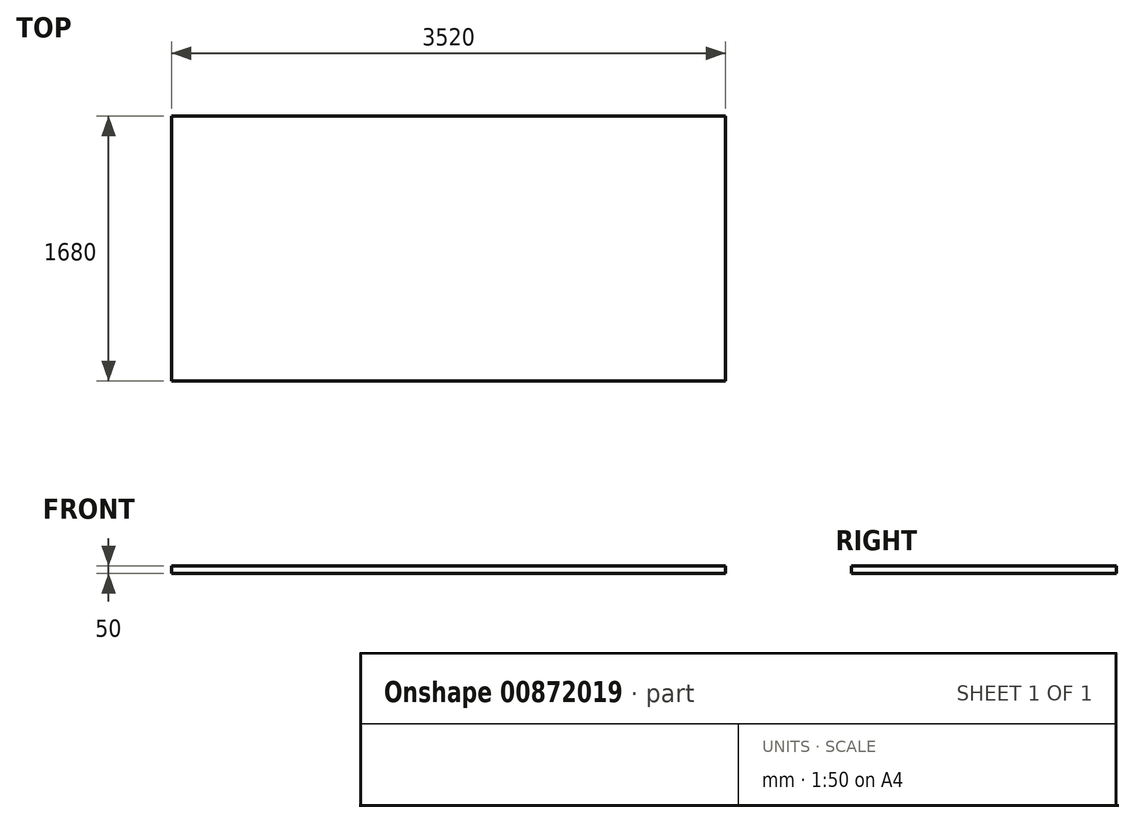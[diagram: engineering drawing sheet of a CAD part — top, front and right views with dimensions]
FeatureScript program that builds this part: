
annotation { "Feature Type Name" : "Feature", "Feature Type Description" : "" }
export const myFeature = defineFeature(function(context is Context, id is Id, definition is map)
    precondition{}
    {
        {
            var Q0;
            Q0=qCreatedBy(makeId("Top.planeOp"),FACE);
            var sketch = newSketch(context, id + "F0", { "sketchPlane" : qUnion([Q0])});
            skLineSegment(sketch, "E0.bottom", {"start": v(1710.63, 817.13) * mm, "end": v(-1809.37, 817.13) * mm});
            skLineSegment(sketch, "E0.top", {"start": v(1710.63, -862.87) * mm, "end": v(-1809.37, -862.87) * mm});
            skLineSegment(sketch, "E0.left", {"start": v(1710.63, 817.13) * mm, "end": v(1710.63, -862.87) * mm});
            skLineSegment(sketch, "E0.right", {"start": v(-1809.37, 817.13) * mm, "end": v(-1809.37, -862.87) * mm});
            skSolve(sketch);
        }
        {
            var Q0;
            Q0=makeQuery(id+"F0.imprint","IMPRINT",FACE,{"disambiguationData":[TD([[makeQuery(id+"F0.imprint","IMPRINT",EDGE,{"derivedFrom":sQuery(id+"F0.wireOp",EDGE,"E0.bottom")}),1.0]])]});
            extrude(context, id + "F1", {"entities" : qUnion([Q0]), "depth" : 50 * mm, "offsetDistance" : 25 * mm});
        }
    });
